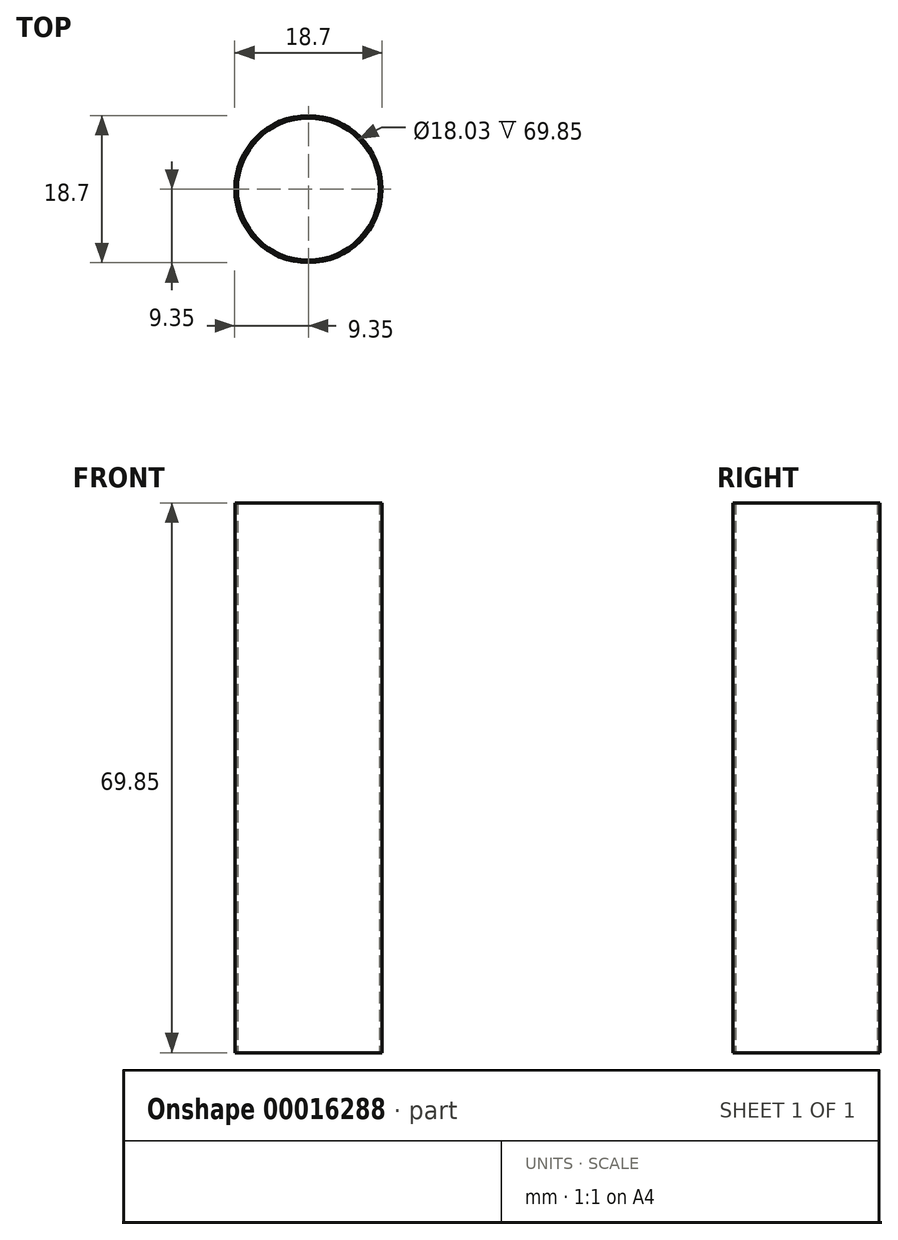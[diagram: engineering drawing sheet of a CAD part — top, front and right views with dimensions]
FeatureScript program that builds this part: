
annotation { "Feature Type Name" : "Feature", "Feature Type Description" : "" }
export const myFeature = defineFeature(function(context is Context, id is Id, definition is map)
    precondition{}
    {
        {
            var Q0;
            Q0=qCreatedBy(makeId("Front.planeOp"),FACE);
            var sketch = newSketch(context, id + "F0", { "sketchPlane" : qUnion([Q0])});
            skLineSegment(sketch, "E0", {"start": v(0, 0) * mm, "end": v(9.02, 0) * mm});
            skLineSegment(sketch, "E1", {"start": v(9.02, 0) * mm, "end": v(9.02, 69.85) * mm});
            skLineSegment(sketch, "E2", {"start": v(9.02, 69.85) * mm, "end": v(9.35, 69.85) * mm});
            skLineSegment(sketch, "E3", {"start": v(9.35, 69.85) * mm, "end": v(9.35, 0) * mm});
            skLineSegment(sketch, "E4", {"start": v(9.35, 0) * mm, "end": v(9.02, 0) * mm});
            skLineSegment(sketch, "E5", {"start": v(0, 0) * mm, "end": v(0, 69.85) * mm});
            skLineSegment(sketch, "E6", {"start": v(0, 69.85) * mm, "end": v(9.02, 69.85) * mm});
            skSolve(sketch);
        }
        {
            var Q0;
            Q0=makeQuery(id+"F0.imprint","IMPRINT",FACE,{"disambiguationData":[TD([[makeQuery(id+"F0.imprint","IMPRINT",EDGE,{"derivedFrom":sQuery(id+"F0.wireOp",EDGE,"E1")}),-1.0]])]});
            var Q1;
            Q1=sQuery(id+"F0.wireOp",EDGE,"E5");
            revolve(context, id + "F1", {"entities" : qUnion([Q0]), "axis" : qUnion([Q1]), "revolveType" : RevolveType.FULL});
        }
        {
            var Q0;
            Q0=qCreatedBy(makeId("Top.planeOp"),FACE);
            var sketch = newSketch(context, id + "F2", { "sketchPlane" : qUnion([Q0])});
            skCircle(sketch, "E7.0", {"center": v(0, 0) * mm, "radius": 9.35 * mm});
            skLineSegment(sketch, "E8", {"start": v(0, 0) * mm, "end": v(0, 9.35) * mm});
            skLineSegment(sketch, "E9", {"start": v(0, 0) * mm, "end": v(0, -9.35) * mm});
            skLineSegment(sketch, "E10", {"start": v(0, 0) * mm, "end": v(-4.67, 8.1) * mm});
            skLineSegment(sketch, "E11.MirrorCS", {"start": v(0, 0) * mm, "end": v(4.67, 8.1) * mm});
            skLineSegment(sketch, "E12", {"start": v(-4.67, 8.1) * mm, "end": v(0, 10.8) * mm});
            skLineSegment(sketch, "E13", {"start": v(0, 10.8) * mm, "end": v(0, 9.35) * mm});
            skCircle(sketch, "E14.1.0", {"center": v(-9.35, 16.19) * mm, "radius": 9.35 * mm});
            skLineSegment(sketch, "E14.1.3", {"start": v(-9.35, 16.19) * mm, "end": v(-1.25, 11.52) * mm});
            skLineSegment(sketch, "E14.1.5", {"start": v(-9.35, 16.19) * mm, "end": v(-17.44, 20.86) * mm});
            skLineSegment(sketch, "E14.1.8", {"start": v(-9.35, 16.19) * mm, "end": v(0, 16.19) * mm});
            skLineSegment(sketch, "E14.1.10", {"start": v(-9.35, 16.19) * mm, "end": v(-4.67, 8.1) * mm});
            skLineSegment(sketch, "E14.1.11", {"start": v(0, 16.19) * mm, "end": v(0, 10.8) * mm});
            skLineSegment(sketch, "E14.1.15", {"start": v(0, 10.8) * mm, "end": v(-1.25, 11.52) * mm});
            skCircle(sketch, "E14.2.0", {"center": v(9.35, 16.19) * mm, "radius": 9.35 * mm});
            skLineSegment(sketch, "E14.2.3", {"start": v(9.35, 16.19) * mm, "end": v(1.25, 11.52) * mm});
            skLineSegment(sketch, "E14.2.5", {"start": v(9.35, 16.19) * mm, "end": v(17.44, 20.86) * mm});
            skLineSegment(sketch, "E14.2.8", {"start": v(9.35, 16.19) * mm, "end": v(4.67, 8.1) * mm});
            skLineSegment(sketch, "E14.2.10", {"start": v(9.35, 16.19) * mm, "end": v(0, 16.19) * mm});
            skLineSegment(sketch, "E14.2.11", {"start": v(4.67, 8.1) * mm, "end": v(0, 10.8) * mm});
            skLineSegment(sketch, "E14.2.15", {"start": v(0, 10.8) * mm, "end": v(1.25, 11.52) * mm});
            skPoint(sketch, "E14.center", {"position": v(0, 10.8) * mm});
            skLineSegment(sketch, "E14.anchor1", {"start": v(0, 10.8) * mm, "end": v(0, 0) * mm, "construction": true});
            skLineSegment(sketch, "E14.anchor2", {"start": v(0, 10.8) * mm, "end": v(9.35, 16.19) * mm, "construction": true});
            skCircle(sketch, "E15", {"center": v(0, 10.8) * mm, "radius": 20.26 * mm});
            skCircle(sketch, "E16", {"center": v(0, 10.8) * mm, "radius": 20.79 * mm});
            skLineSegment(sketch, "E17", {"start": v(0, 0) * mm, "end": v(-9.03, 2.42) * mm});
            skLineSegment(sketch, "E18", {"start": v(-9.03, 2.42) * mm, "end": v(-9.44, 0.89) * mm});
            skLineSegment(sketch, "E19", {"start": v(-9.44, 0.89) * mm, "end": v(-0.41, -1.53) * mm});
            skLineSegment(sketch, "E20", {"start": v(-0.41, -1.53) * mm, "end": v(0, 0) * mm});
            skLineSegment(sketch, "E21", {"start": v(-9.03, 2.42) * mm, "end": v(-8.62, 3.95) * mm});
            skLineSegment(sketch, "E22", {"start": v(-8.62, 3.95) * mm, "end": v(0.41, 1.53) * mm});
            skLineSegment(sketch, "E23", {"start": v(0.41, 1.53) * mm, "end": v(0, 0) * mm});
            skLineSegment(sketch, "E24.MirrorCS", {"start": v(-9.44, 0.89) * mm, "end": v(-18.47, 3.3) * mm});
            skLineSegment(sketch, "E25.MirrorCS", {"start": v(-18.06, 4.84) * mm, "end": v(-9.03, 2.42) * mm});
            skLineSegment(sketch, "E26.MirrorCS", {"start": v(-8.62, 3.95) * mm, "end": v(-17.65, 6.37) * mm});
            skLineSegment(sketch, "E27.MirrorCS", {"start": v(-17.65, 6.37) * mm, "end": v(-18.06, 4.84) * mm});
            skLineSegment(sketch, "E28.MirrorCS", {"start": v(-18.47, 3.3) * mm, "end": v(-18.06, 4.84) * mm});
            skLineSegment(sketch, "E29", {"start": v(0, 0) * mm, "end": v(-9.35, 0) * mm});
            skSolve(sketch);
        }
    });
